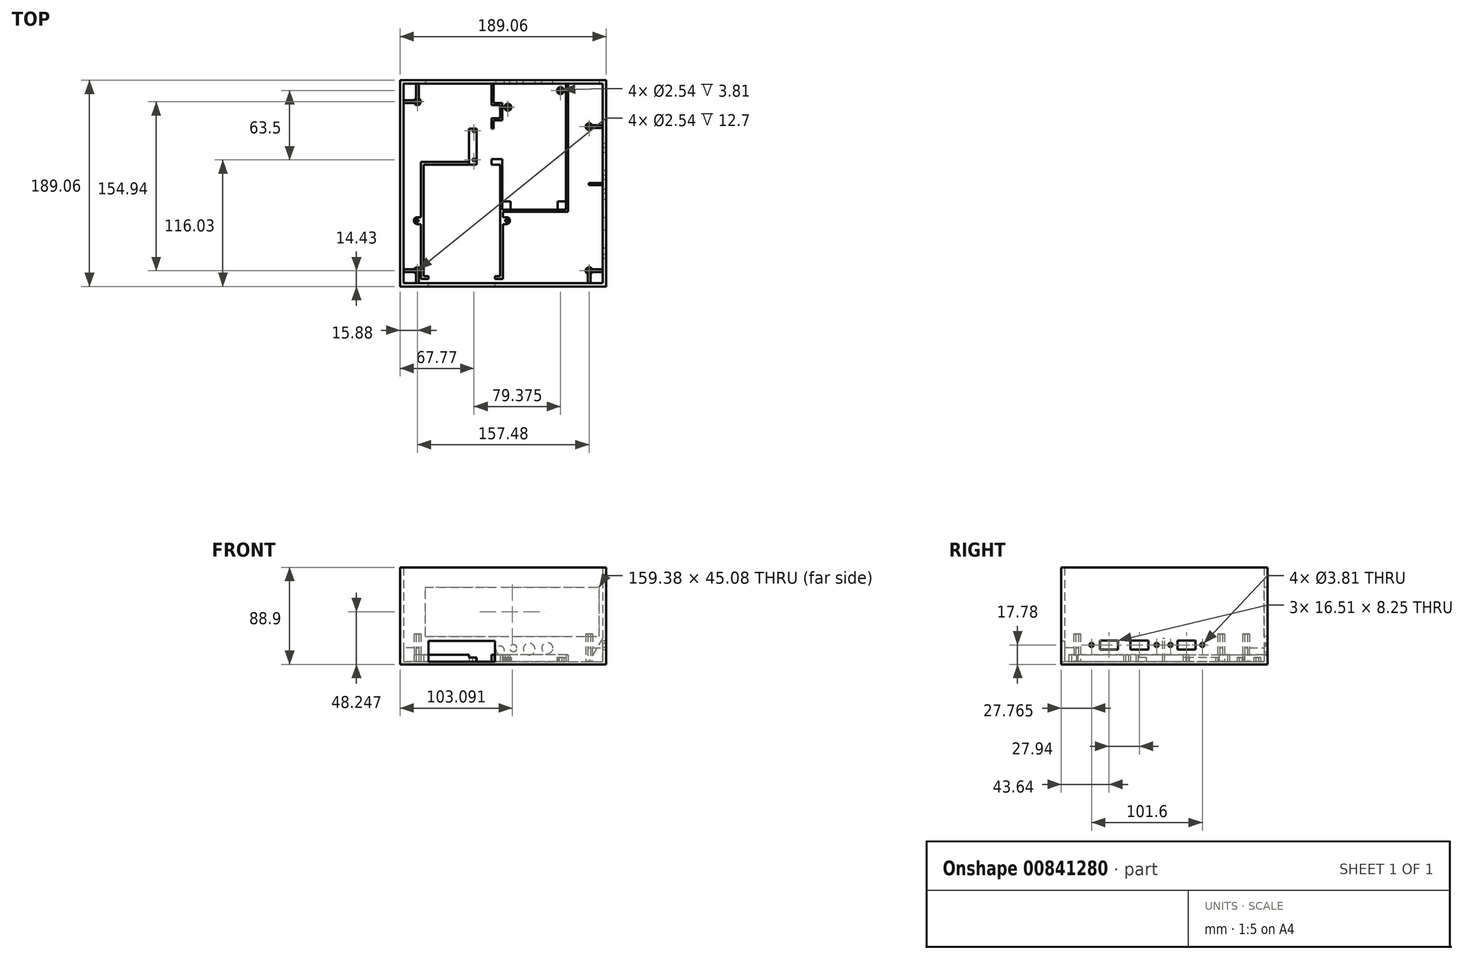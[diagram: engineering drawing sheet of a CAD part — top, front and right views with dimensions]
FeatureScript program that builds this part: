
annotation { "Feature Type Name" : "Feature", "Feature Type Description" : "" }
export const myFeature = defineFeature(function(context is Context, id is Id, definition is map)
    precondition{}
    {
        {
            var Q0;
            Q0=qCreatedBy(makeId("Top.planeOp"),FACE);
            var sketch = newSketch(context, id + "F0", { "sketchPlane" : qUnion([Q0])});
            skLineSegment(sketch, "E0.bottom", {"start": v(-6.35, 10.16) * mm, "end": v(163.65, 10.16) * mm});
            skLineSegment(sketch, "E0.top", {"start": v(-6.35, -159.84) * mm, "end": v(163.65, -159.84) * mm});
            skLineSegment(sketch, "E0.left", {"start": v(-6.35, 10.16) * mm, "end": v(-6.35, -159.84) * mm});
            skLineSegment(sketch, "E0.right", {"start": v(163.65, 10.16) * mm, "end": v(163.65, -159.84) * mm});
            skPoint(sketch, "E1", {"position": v(0, -154.94) * mm});
            skPoint(sketch, "E2", {"position": v(157.48, -22.86) * mm});
            skPoint(sketch, "E3", {"position": v(157.48, -154.94) * mm});
            skCircle(sketch, "E4", {"center": v(0, -154.94) * mm, "radius": 3.18 * mm});
            skCircle(sketch, "E5", {"center": v(0, 0) * mm, "radius": 3.18 * mm});
            skCircle(sketch, "E6", {"center": v(157.48, -22.86) * mm, "radius": 3.18 * mm});
            skCircle(sketch, "E7", {"center": v(157.48, -154.94) * mm, "radius": 3.18 * mm});
            skSolve(sketch);
        }
        {
            var Q0;
            Q0=qCreatedBy(makeId("Top.planeOp"),FACE);
            var sketch = newSketch(context, id + "F1", { "sketchPlane" : qUnion([Q0])});
            skLineSegment(sketch, "E8.0", {"start": v(-12.7, 16.51) * mm, "end": v(170, 16.51) * mm});
            skLineSegment(sketch, "E8.1", {"start": v(-12.7, 16.51) * mm, "end": v(-12.7, -166.2) * mm});
            skLineSegment(sketch, "E8.2", {"start": v(-12.7, -166.2) * mm, "end": v(170, -166.2) * mm});
            skLineSegment(sketch, "E8.3", {"start": v(170, 16.51) * mm, "end": v(170, -166.2) * mm});
            skLineSegment(sketch, "E9.0", {"start": v(-15.88, 19.69) * mm, "end": v(173.18, 19.69) * mm});
            skLineSegment(sketch, "E9.1", {"start": v(-15.88, 19.69) * mm, "end": v(-15.88, -169.37) * mm});
            skLineSegment(sketch, "E9.2", {"start": v(-15.88, -169.37) * mm, "end": v(173.18, -169.37) * mm});
            skLineSegment(sketch, "E9.3", {"start": v(173.18, 19.69) * mm, "end": v(173.18, -169.37) * mm});
            skSolve(sketch);
        }
        {
            var Q0;
            Q0=qSketchRegion(id+"F1",true);
            extrude(context, id + "F2", {"entities" : qUnion([Q0]), "depth" : 86.36 * mm, "offsetDistance" : 25.4 * mm});
        }
        {
            var Q0;
            Q0=qCreatedBy(makeId("Top.planeOp"),FACE);
            var sketch = newSketch(context, id + "F3", { "sketchPlane" : qUnion([Q0])});
            skLineSegment(sketch, "E10.bottom", {"start": v(135.08, -97.79) * mm, "end": v(135.08, 15.24) * mm, "construction": true});
            skLineSegment(sketch, "E10.top", {"start": v(79.2, -18.41) * mm, "end": v(79.2, 0) * mm, "construction": true});
            skLineSegment(sketch, "E10.left", {"start": v(135.08, 15.24) * mm, "end": v(79.2, 15.24) * mm, "construction": true});
            skLineSegment(sketch, "E10.right", {"start": v(135.08, -97.79) * mm, "end": v(79.2, -97.79) * mm, "construction": true});
            skCircle(sketch, "E11", {"center": v(131.27, 10.16) * mm, "radius": 1.27 * mm});
            skCircle(sketch, "E12", {"center": v(131.27, 10.16) * mm, "radius": 3.18 * mm});
            skLineSegment(sketch, "E13", {"start": v(79.2, 15.24) * mm, "end": v(71.07, 15.24) * mm, "construction": true});
            skLineSegment(sketch, "E14", {"start": v(71.07, 15.24) * mm, "end": v(71.07, 0) * mm, "construction": true});
            skLineSegment(sketch, "E15", {"start": v(71.07, 0) * mm, "end": v(79.2, 0) * mm, "construction": true});
            skLineSegment(sketch, "E16", {"start": v(79.2, -18.41) * mm, "end": v(71.07, -18.41) * mm, "construction": true});
            skLineSegment(sketch, "E17", {"start": v(71.07, -18.41) * mm, "end": v(71.07, -50.16) * mm, "construction": true});
            skLineSegment(sketch, "E18", {"start": v(71.07, -50.16) * mm, "end": v(79.2, -50.16) * mm, "construction": true});
            skCircle(sketch, "E19", {"center": v(83, -5.08) * mm, "radius": 3.18 * mm});
            skCircle(sketch, "E20", {"center": v(83, -5.08) * mm, "radius": 1.27 * mm});
            skLineSegment(sketch, "E21.trimOffspring", {"start": v(79.2, -97.79) * mm, "end": v(79.2, -50.16) * mm, "construction": true});
            skLineSegment(sketch, "E22.0", {"start": v(77.93, -17.14) * mm, "end": v(77.93, -1.27) * mm});
            skLineSegment(sketch, "E22.1", {"start": v(77.93, -17.14) * mm, "end": v(69.8, -17.14) * mm});
            skLineSegment(sketch, "E22.4", {"start": v(77.93, -99.06) * mm, "end": v(77.93, -52.7) * mm});
            skLineSegment(sketch, "E22.5", {"start": v(69.8, -1.27) * mm, "end": v(77.93, -1.27) * mm});
            skLineSegment(sketch, "E22.6", {"start": v(69.8, 16.51) * mm, "end": v(69.8, -1.27) * mm});
            skLineSegment(sketch, "E22.8", {"start": v(136.35, 16.51) * mm, "end": v(69.8, 16.51) * mm});
            skLineSegment(sketch, "E22.9", {"start": v(136.35, -99.06) * mm, "end": v(136.35, 16.51) * mm});
            skLineSegment(sketch, "E22.10", {"start": v(136.35, -99.06) * mm, "end": v(77.93, -99.06) * mm});
            skLineSegment(sketch, "E23.bottom", {"start": v(77.93, -99.06) * mm, "end": v(77.93, -91.44) * mm});
            skLineSegment(sketch, "E23.top", {"start": v(85.55, -99.06) * mm, "end": v(85.55, -91.44) * mm});
            skLineSegment(sketch, "E23.left", {"start": v(77.93, -99.06) * mm, "end": v(85.55, -99.06) * mm});
            skLineSegment(sketch, "E23.right", {"start": v(77.93, -91.44) * mm, "end": v(85.55, -91.44) * mm});
            skLineSegment(sketch, "E24.bottom", {"start": v(136.35, -99.06) * mm, "end": v(136.35, -91.44) * mm});
            skLineSegment(sketch, "E24.top", {"start": v(128.73, -99.06) * mm, "end": v(128.73, -91.44) * mm});
            skLineSegment(sketch, "E24.left", {"start": v(136.35, -99.06) * mm, "end": v(128.73, -99.06) * mm});
            skLineSegment(sketch, "E24.right", {"start": v(136.35, -91.44) * mm, "end": v(128.73, -91.44) * mm});
            skLineSegment(sketch, "E25.0", {"start": v(138.25, -100.96) * mm, "end": v(76.02, -100.96) * mm});
            skLineSegment(sketch, "E25.1", {"start": v(138.25, -100.96) * mm, "end": v(138.25, 18.42) * mm});
            skLineSegment(sketch, "E25.2", {"start": v(76.02, -100.96) * mm, "end": v(76.02, -57.78) * mm});
            skLineSegment(sketch, "E25.3", {"start": v(138.25, 18.42) * mm, "end": v(67.9, 18.42) * mm});
            skLineSegment(sketch, "E25.4", {"start": v(67.9, 18.42) * mm, "end": v(67.9, -3.17) * mm});
            skLineSegment(sketch, "E25.5", {"start": v(67.9, -3.17) * mm, "end": v(76.02, -3.17) * mm});
            skLineSegment(sketch, "E25.7", {"start": v(67.9, -15.24) * mm, "end": v(67.9, -24.76) * mm});
            skLineSegment(sketch, "E25.8", {"start": v(76.02, -15.24) * mm, "end": v(67.9, -15.24) * mm});
            skLineSegment(sketch, "E25.9", {"start": v(76.02, -15.24) * mm, "end": v(76.02, -3.17) * mm});
            skLineSegment(sketch, "E26", {"start": v(76.02, -57.78) * mm, "end": v(47.45, -57.78) * mm});
            skLineSegment(sketch, "E27", {"start": v(69.8, -17.14) * mm, "end": v(69.8, -27.94) * mm});
            skCircle(sketch, "E28", {"center": v(51.9, -53.34) * mm, "radius": 1.27 * mm});
            skLineSegment(sketch, "E29", {"start": v(54.43, -52.7) * mm, "end": v(54.43, -27.94) * mm});
            skLineSegment(sketch, "E30", {"start": v(54.43, -52.7) * mm, "end": v(77.93, -52.7) * mm});
            skLineSegment(sketch, "E31", {"start": v(54.43, -27.94) * mm, "end": v(69.8, -27.94) * mm});
            skCircle(sketch, "E32", {"center": v(51.9, -26.67) * mm, "radius": 1.27 * mm});
            skLineSegment(sketch, "E33", {"start": v(47.45, -57.78) * mm, "end": v(47.45, -24.76) * mm});
            skLineSegment(sketch, "E34", {"start": v(47.45, -24.76) * mm, "end": v(67.9, -24.76) * mm});
            skLineSegment(sketch, "E35", {"start": v(54.43, -52.7) * mm, "end": v(54.43, -57.78) * mm});
            skLineSegment(sketch, "E36", {"start": v(54.43, -27.94) * mm, "end": v(54.43, -24.76) * mm});
            skLineSegment(sketch, "E37", {"start": v(136.35, 16.51) * mm, "end": v(138.25, 16.51) * mm});
            skLineSegment(sketch, "E38", {"start": v(69.8, 16.51) * mm, "end": v(67.9, 16.51) * mm});
            skLineSegment(sketch, "E39", {"start": v(67.9, -52.7) * mm, "end": v(67.9, -57.78) * mm});
            skLineSegment(sketch, "E40", {"start": v(67.9, -24.76) * mm, "end": v(69.8, -24.76) * mm});
            skSolve(sketch);
        }
        {
            var Q0;
            Q0=qCreatedBy(makeId("Top.planeOp"),FACE);
            var sketch = newSketch(context, id + "F4", { "sketchPlane" : qUnion([Q0])});
            skLineSegment(sketch, "E41.bottom", {"start": v(5.66, -57.78) * mm, "end": v(76.02, -57.78) * mm});
            skLineSegment(sketch, "E41.top", {"start": v(5.66, -159.84) * mm, "end": v(76.02, -159.84) * mm});
            skLineSegment(sketch, "E41.left", {"start": v(5.66, -57.78) * mm, "end": v(5.66, -159.84) * mm});
            skLineSegment(sketch, "E41.right", {"start": v(76.02, -57.78) * mm, "end": v(76.02, -159.84) * mm});
            skLineSegment(sketch, "E42.0", {"start": v(3.12, -55.24) * mm, "end": v(47.45, -55.24) * mm});
            skLineSegment(sketch, "E42.1", {"start": v(3.12, -55.24) * mm, "end": v(3.12, -105.86) * mm});
            skLineSegment(sketch, "E42.2", {"start": v(3.12, -162.38) * mm, "end": v(10.36, -162.38) * mm});
            skLineSegment(sketch, "E42.3", {"start": v(78.56, -100.96) * mm, "end": v(78.56, -105.86) * mm});
            skLineSegment(sketch, "E43", {"start": v(47.45, -55.24) * mm, "end": v(47.45, -57.78) * mm});
            skLineSegment(sketch, "E44", {"start": v(76.02, -100.96) * mm, "end": v(78.56, -100.96) * mm});
            skLineSegment(sketch, "E45", {"start": v(10.36, -162.38) * mm, "end": v(10.36, -159.84) * mm});
            skLineSegment(sketch, "E46", {"start": v(40.84, -162.38) * mm, "end": v(40.84, -159.84) * mm, "construction": true});
            skLineSegment(sketch, "E47.MirrorCS", {"start": v(71.32, -162.38) * mm, "end": v(71.32, -159.84) * mm});
            skLineSegment(sketch, "E48.trimOffspring", {"start": v(71.32, -162.38) * mm, "end": v(78.56, -162.38) * mm});
            skArc(sketch, "E49", {"start": v(81.74, -112.21) * mm, "mid": v(84.91, -109.04) * mm, "end": v(81.74, -105.86) * mm});
            skLineSegment(sketch, "E50", {"start": v(81.74, -105.86) * mm, "end": v(81.74, -112.21) * mm, "construction": true});
            skLineSegment(sketch, "E51", {"start": v(81.74, -112.21) * mm, "end": v(78.56, -112.21) * mm});
            skLineSegment(sketch, "E52", {"start": v(81.74, -105.86) * mm, "end": v(78.56, -105.86) * mm});
            skLineSegment(sketch, "E53.trimOffspring", {"start": v(78.56, -112.21) * mm, "end": v(78.56, -162.38) * mm});
            skLineSegment(sketch, "E54.MirrorCS", {"start": v(-0.05, -105.86) * mm, "end": v(3.12, -105.86) * mm});
            skLineSegment(sketch, "E55.MirrorCS", {"start": v(-0.05, -112.21) * mm, "end": v(3.12, -112.21) * mm});
            skArc(sketch, "E56.MirrorCS", {"start": v(-0.05, -112.21) * mm, "mid": v(-3.23, -109.04) * mm, "end": v(-0.05, -105.86) * mm});
            skLineSegment(sketch, "E57.trimOffspring", {"start": v(3.12, -112.21) * mm, "end": v(3.12, -162.38) * mm});
            skCircle(sketch, "E58", {"center": v(81.74, -109.04) * mm, "radius": 1.27 * mm});
            skCircle(sketch, "E59", {"center": v(-0.05, -109.04) * mm, "radius": 1.27 * mm});
            skSolve(sketch);
        }
        {
            var Q0;
            Q0=qCreatedBy(makeId("Top.planeOp"),FACE);
            var sketch = newSketch(context, id + "F5", { "sketchPlane" : qUnion([Q0])});
            skLineSegment(sketch, "E60.bottom", {"start": v(-15.88, 19.69) * mm, "end": v(173.18, 19.69) * mm});
            skLineSegment(sketch, "E60.top", {"start": v(-15.88, -169.37) * mm, "end": v(173.18, -169.37) * mm});
            skLineSegment(sketch, "E60.left", {"start": v(-15.88, 19.69) * mm, "end": v(-15.88, -169.37) * mm});
            skLineSegment(sketch, "E60.right", {"start": v(173.18, 19.69) * mm, "end": v(173.18, -169.37) * mm});
            skSolve(sketch);
        }
        {
            var Q0;
            Q0=qSketchRegion(id+"F5",true);
            extrude(context, id + "F6", {"entities" : qUnion([Q0]), "operationType" : NewBodyOperationType.ADD, "oppositeDirection" : true, "depth" : 2.54 * mm, "offsetDistance" : 25.4 * mm});
        }
        {
            var Q0;
            Q0=qCreatedBy(makeId("Top.planeOp"),FACE);
            var sketch = newSketch(context, id + "F7", { "sketchPlane" : qUnion([Q0])});
            skLineSegment(sketch, "E61.bottom", {"start": v(77.93, -91.44) * mm, "end": v(85.55, -91.44) * mm});
            skLineSegment(sketch, "E61.top", {"start": v(77.93, -99.06) * mm, "end": v(85.55, -99.06) * mm});
            skLineSegment(sketch, "E61.left", {"start": v(77.93, -91.44) * mm, "end": v(77.93, -99.06) * mm});
            skLineSegment(sketch, "E61.right", {"start": v(85.55, -91.44) * mm, "end": v(85.55, -99.06) * mm});
            skLineSegment(sketch, "E62.bottom", {"start": v(128.73, -91.44) * mm, "end": v(136.35, -91.44) * mm});
            skLineSegment(sketch, "E62.top", {"start": v(128.73, -99.06) * mm, "end": v(136.35, -99.06) * mm});
            skLineSegment(sketch, "E62.left", {"start": v(128.73, -91.44) * mm, "end": v(128.73, -99.06) * mm});
            skLineSegment(sketch, "E62.right", {"start": v(136.35, -91.44) * mm, "end": v(136.35, -99.06) * mm});
            skCircle(sketch, "E63.0", {"center": v(83, -5.08) * mm, "radius": 3.18 * mm});
            skCircle(sketch, "E63.1", {"center": v(131.27, 10.16) * mm, "radius": 3.18 * mm});
            skCircle(sketch, "E64.0", {"center": v(83, -5.08) * mm, "radius": 1.27 * mm});
            skCircle(sketch, "E64.1", {"center": v(131.27, 10.16) * mm, "radius": 1.27 * mm});
            skLineSegment(sketch, "E65.bottom", {"start": v(47.45, -24.76) * mm, "end": v(54.43, -24.76) * mm});
            skLineSegment(sketch, "E65.top", {"start": v(47.45, -57.78) * mm, "end": v(54.43, -57.78) * mm});
            skLineSegment(sketch, "E65.left", {"start": v(47.45, -24.76) * mm, "end": v(47.45, -57.78) * mm});
            skLineSegment(sketch, "E65.right", {"start": v(54.43, -24.76) * mm, "end": v(54.43, -57.78) * mm});
            skCircle(sketch, "E66.1", {"center": v(51.9, -26.67) * mm, "radius": 1.27 * mm});
            skCircle(sketch, "E66.2", {"center": v(51.9, -53.34) * mm, "radius": 1.27 * mm});
            skSolve(sketch);
        }
        {
            var Q0;
            Q0=qSketchRegion(id+"F7",true);
            extrude(context, id + "F8", {"entities" : qUnion([Q0]), "operationType" : NewBodyOperationType.ADD, "depth" : 3.8 * mm, "offsetDistance" : 25.4 * mm});
        }
        {
            var Q0;
            Q0=qCreatedBy(makeId("Top.planeOp"),FACE);
            var sketch = newSketch(context, id + "F9", { "sketchPlane" : qUnion([Q0])});
            skLineSegment(sketch, "E67.0", {"start": v(67.9, -15.24) * mm, "end": v(67.9, -24.76) * mm});
            skLineSegment(sketch, "E67.1", {"start": v(67.9, -24.76) * mm, "end": v(69.8, -24.76) * mm});
            skLineSegment(sketch, "E67.2", {"start": v(69.8, -17.14) * mm, "end": v(69.8, -24.76) * mm});
            skLineSegment(sketch, "E67.3", {"start": v(76.02, -15.24) * mm, "end": v(67.9, -15.24) * mm});
            skLineSegment(sketch, "E67.4", {"start": v(77.93, -17.14) * mm, "end": v(69.8, -17.14) * mm});
            skLineSegment(sketch, "E67.5", {"start": v(77.93, -17.14) * mm, "end": v(77.93, -1.27) * mm});
            skLineSegment(sketch, "E67.6", {"start": v(76.02, -15.24) * mm, "end": v(76.02, -3.17) * mm});
            skLineSegment(sketch, "E67.7", {"start": v(69.8, -1.27) * mm, "end": v(77.93, -1.27) * mm});
            skLineSegment(sketch, "E67.8", {"start": v(67.9, -3.17) * mm, "end": v(76.02, -3.17) * mm});
            skLineSegment(sketch, "E67.9", {"start": v(67.9, 16.51) * mm, "end": v(67.9, -3.17) * mm});
            skLineSegment(sketch, "E67.10", {"start": v(69.8, 16.51) * mm, "end": v(69.8, -1.27) * mm});
            skLineSegment(sketch, "E67.13", {"start": v(136.35, -99.06) * mm, "end": v(136.35, 16.51) * mm});
            skLineSegment(sketch, "E67.14", {"start": v(138.25, -100.96) * mm, "end": v(138.25, 16.51) * mm});
            skLineSegment(sketch, "E67.15", {"start": v(136.35, -99.06) * mm, "end": v(77.93, -99.06) * mm});
            skLineSegment(sketch, "E67.16", {"start": v(138.25, -100.96) * mm, "end": v(78.56, -100.96) * mm});
            skLineSegment(sketch, "E67.17", {"start": v(78.56, -100.96) * mm, "end": v(78.56, -105.86) * mm});
            skLineSegment(sketch, "E67.18", {"start": v(81.74, -105.86) * mm, "end": v(78.56, -105.86) * mm});
            skArc(sketch, "E67.19", {"start": v(81.74, -112.21) * mm, "mid": v(84.91, -109.04) * mm, "end": v(81.74, -105.86) * mm});
            skLineSegment(sketch, "E67.20.1", {"start": v(76.02, -100.96) * mm, "end": v(76.02, -159.84) * mm});
            skLineSegment(sketch, "E67.20.2", {"start": v(76.02, -159.84) * mm, "end": v(71.32, -159.84) * mm});
            skLineSegment(sketch, "E67.20.3", {"start": v(71.32, -159.84) * mm, "end": v(71.32, -162.38) * mm});
            skLineSegment(sketch, "E67.20.4", {"start": v(71.32, -162.38) * mm, "end": v(78.56, -162.38) * mm});
            skLineSegment(sketch, "E67.20.5", {"start": v(78.56, -162.38) * mm, "end": v(78.56, -112.21) * mm});
            skLineSegment(sketch, "E67.20.6", {"start": v(78.56, -112.21) * mm, "end": v(81.74, -112.21) * mm});
            skArc(sketch, "E67.20.7", {"start": v(81.74, -112.21) * mm, "mid": v(84.91, -109.04) * mm, "end": v(81.74, -105.86) * mm});
            skLineSegment(sketch, "E67.20.8", {"start": v(81.74, -105.86) * mm, "end": v(78.56, -105.86) * mm});
            skLineSegment(sketch, "E67.20.9", {"start": v(78.56, -105.86) * mm, "end": v(78.56, -100.96) * mm});
            skLineSegment(sketch, "E67.21.0", {"start": v(47.45, -57.78) * mm, "end": v(47.45, -55.24) * mm});
            skLineSegment(sketch, "E67.21.1", {"start": v(47.45, -55.24) * mm, "end": v(3.12, -55.24) * mm});
            skLineSegment(sketch, "E67.21.2", {"start": v(3.12, -55.24) * mm, "end": v(3.12, -105.86) * mm});
            skLineSegment(sketch, "E67.21.3", {"start": v(3.12, -105.86) * mm, "end": v(-0.05, -105.86) * mm});
            skArc(sketch, "E67.21.4", {"start": v(-0.05, -105.86) * mm, "mid": v(-3.23, -109.04) * mm, "end": v(-0.05, -112.21) * mm});
            skLineSegment(sketch, "E67.21.5", {"start": v(-0.05, -112.21) * mm, "end": v(3.12, -112.21) * mm});
            skLineSegment(sketch, "E67.21.6", {"start": v(3.12, -112.21) * mm, "end": v(3.12, -162.38) * mm});
            skLineSegment(sketch, "E67.21.7", {"start": v(3.12, -162.38) * mm, "end": v(10.36, -162.38) * mm});
            skLineSegment(sketch, "E67.21.8", {"start": v(10.36, -162.38) * mm, "end": v(10.36, -159.84) * mm});
            skLineSegment(sketch, "E67.21.9", {"start": v(10.36, -159.84) * mm, "end": v(5.66, -159.84) * mm});
            skLineSegment(sketch, "E67.21.10", {"start": v(5.66, -159.84) * mm, "end": v(5.66, -57.78) * mm});
            skLineSegment(sketch, "E67.21.11", {"start": v(5.66, -57.78) * mm, "end": v(47.45, -57.78) * mm});
            skLineSegment(sketch, "E67.22", {"start": v(76.02, -100.96) * mm, "end": v(76.02, -57.78) * mm});
            skLineSegment(sketch, "E67.23", {"start": v(77.93, -99.06) * mm, "end": v(77.93, -52.7) * mm});
            skLineSegment(sketch, "E67.24", {"start": v(67.9, -52.7) * mm, "end": v(77.93, -52.7) * mm});
            skLineSegment(sketch, "E67.25", {"start": v(67.9, -52.7) * mm, "end": v(67.9, -57.78) * mm});
            skLineSegment(sketch, "E67.26", {"start": v(76.02, -57.78) * mm, "end": v(67.9, -57.78) * mm});
            skPoint(sketch, "E68.orphan", {"position": v(69.8, -27.94) * mm});
            skPoint(sketch, "E69.orphan", {"position": v(54.43, -52.7) * mm});
            skPoint(sketch, "E70.orphan", {"position": v(47.45, -57.78) * mm});
            skPoint(sketch, "E71.orphan", {"position": v(76.02, -100.96) * mm});
            skLineSegment(sketch, "E72.0", {"start": v(67.9, 16.51) * mm, "end": v(69.8, 16.51) * mm});
            skPoint(sketch, "E73.orphan", {"position": v(-12.7, 16.51) * mm});
            skPoint(sketch, "E74.orphan", {"position": v(170, 16.51) * mm});
            skPoint(sketch, "E75.orphan", {"position": v(138.25, 18.42) * mm});
            skPoint(sketch, "E76.orphan", {"position": v(67.9, 18.42) * mm});
            skLineSegment(sketch, "E77.trimOffspring", {"start": v(136.35, 16.51) * mm, "end": v(138.25, 16.51) * mm});
            skCircle(sketch, "E78.0", {"center": v(-0.05, -109.04) * mm, "radius": 1.27 * mm});
            skCircle(sketch, "E78.1", {"center": v(81.74, -109.04) * mm, "radius": 1.27 * mm});
            skSolve(sketch);
        }
        {
            var Q0;
            Q0=qSketchRegion(id+"F9",true);
            extrude(context, id + "F10", {"entities" : qUnion([Q0]), "operationType" : NewBodyOperationType.ADD, "depth" : 6.35 * mm, "offsetDistance" : 25.4 * mm});
        }
        {
            var Q0;
            Q0=makeQuery(id+"F6.boolean.opBoolean","MERGE",FACE,{"derivedFrom":[makeQuery(id+"F2.opExtrude","SWEPT_FACE",FACE,{"disambiguationData":[OSD([sQuery(id+"F1.wireOp",EDGE,"E9.0")])]}),makeQuery(id+"F6.opExtrude","SWEPT_FACE",FACE,{"disambiguationData":[OSD([sQuery(id+"F5.wireOp",EDGE,"E60.bottom")])]})]});
            var sketch = newSketch(context, id + "F11", { "sketchPlane" : qUnion([Q0])});
            skCircle(sketch, "E79", {"center": v(-119.2, 12.32) * mm, "radius": 5.08 * mm});
            skCircle(sketch, "E80", {"center": v(-102.56, 11.43) * mm, "radius": 5.4 * mm});
            skCircle(sketch, "E81", {"center": v(-88.09, 12.32) * mm, "radius": 3.18 * mm});
            skCircle(sketch, "E82", {"center": v(-75.9, 10.41) * mm, "radius": 3.81 * mm});
            skLineSegment(sketch, "E83", {"start": v(-54.43, 3.81) * mm, "end": v(-135.08, 3.81) * mm, "construction": true});
            skLineSegment(sketch, "E84", {"start": v(-135.08, 3.81) * mm, "end": v(-135.08, 0) * mm, "construction": true});
            skSolve(sketch);
        }
        {
            var Q0;
            Q0=qSketchRegion(id+"F11",true);
            extrude(context, id + "F12", {"entities" : qUnion([Q0]), "operationType" : NewBodyOperationType.REMOVE, "endBound" : BoundingType.UP_TO_NEXT, "oppositeDirection" : true, "depth" : 25.4 * mm, "offsetDistance" : 25.4 * mm});
        }
        {
            var Q0;
            Q0=makeQuery(id+"F2.opExtrude","SWEPT_FACE",FACE,{"disambiguationData":[OSD([sQuery(id+"F1.wireOp",EDGE,"E8.2")])]});
            var sketch = newSketch(context, id + "F13", { "sketchPlane" : qUnion([Q0])});
            skLineSegment(sketch, "E85.0", {"start": v(-10.36, 6.35) * mm, "end": v(-10.36, 0) * mm});
            skLineSegment(sketch, "E85.1", {"start": v(-71.32, 6.35) * mm, "end": v(-71.32, 0) * mm});
            skLineSegment(sketch, "E86", {"start": v(-10.36, 6.35) * mm, "end": v(-71.32, 6.35) * mm, "construction": true});
            skLineSegment(sketch, "E87", {"start": v(-10.36, 0) * mm, "end": v(-71.32, 0) * mm});
            skLineSegment(sketch, "E88", {"start": v(-10.36, 6.35) * mm, "end": v(-10.36, 19.05) * mm});
            skLineSegment(sketch, "E89", {"start": v(-10.36, 19.05) * mm, "end": v(-71.32, 19.05) * mm});
            skLineSegment(sketch, "E90", {"start": v(-71.32, 19.05) * mm, "end": v(-71.32, 6.35) * mm});
            skLineSegment(sketch, "E91", {"start": v(-16.71, 19.05) * mm, "end": v(-16.71, 0) * mm, "construction": true});
            skLineSegment(sketch, "E92", {"start": v(-17.47, 19.05) * mm, "end": v(-17.47, 0) * mm, "construction": true});
            skLineSegment(sketch, "E93.1.0.0", {"start": v(-28.14, 19.05) * mm, "end": v(-28.14, 0) * mm, "construction": true});
            skLineSegment(sketch, "E93.1.0.1", {"start": v(-28.9, 19.05) * mm, "end": v(-28.9, 0) * mm, "construction": true});
            skLineSegment(sketch, "E93.2.0.0", {"start": v(-39.57, 19.05) * mm, "end": v(-39.57, 0) * mm, "construction": true});
            skLineSegment(sketch, "E93.2.0.1", {"start": v(-40.33, 19.05) * mm, "end": v(-40.33, 0) * mm, "construction": true});
            skLineSegment(sketch, "E93.3.0.0", {"start": v(-51, 19.05) * mm, "end": v(-51, 0) * mm, "construction": true});
            skLineSegment(sketch, "E93.3.0.1", {"start": v(-51.76, 19.05) * mm, "end": v(-51.76, 0) * mm, "construction": true});
            skLineSegment(sketch, "E93.4.0.0", {"start": v(-62.43, 19.05) * mm, "end": v(-62.43, 0) * mm, "construction": true});
            skLineSegment(sketch, "E93.4.0.1", {"start": v(-63.2, 19.05) * mm, "end": v(-63.2, 0) * mm, "construction": true});
            skLineSegment(sketch, "E93.direction1", {"start": v(-17.47, 0) * mm, "end": v(-28.9, 0) * mm, "construction": true});
            skSolve(sketch);
        }
        {
            var Q0;
            {var subQ4=sQuery(id+"F13.wireOp",EDGE,"E85.0");Q0=makeQuery(id+"F13.imprint","IMPRINT",FACE,{"disambiguationData":[TD([[makeQuery(id+"F13.imprint","IMPRINT",EDGE,{"derivedFrom":subQ4}),-1.0]])]});}
            var Q1;
            {var subQ0=sQuery(id+"F13.wireOp",EDGE,"E92");Q1=makeQuery(id+"F13.imprint","IMPRINT",FACE,{"disambiguationData":[TD([[makeQuery(id+"F13.imprint","IMPRINT",EDGE,{"derivedFrom":subQ0}),-1.0]])]});}
            var Q2;
            {var subQ0=sQuery(id+"F13.wireOp",EDGE,"E93.1.0.1");Q2=makeQuery(id+"F13.imprint","IMPRINT",FACE,{"disambiguationData":[TD([[makeQuery(id+"F13.imprint","IMPRINT",EDGE,{"derivedFrom":subQ0}),-1.0]])]});}
            var Q3;
            {var subQ0=sQuery(id+"F13.wireOp",EDGE,"E93.2.0.1");Q3=makeQuery(id+"F13.imprint","IMPRINT",FACE,{"disambiguationData":[TD([[makeQuery(id+"F13.imprint","IMPRINT",EDGE,{"derivedFrom":subQ0}),-1.0]])]});}
            var Q4;
            {var subQ0=sQuery(id+"F13.wireOp",EDGE,"E93.3.0.1");Q4=makeQuery(id+"F13.imprint","IMPRINT",FACE,{"disambiguationData":[TD([[makeQuery(id+"F13.imprint","IMPRINT",EDGE,{"derivedFrom":subQ0}),-1.0]])]});}
            var Q5;
            {var subQ4=sQuery(id+"F13.wireOp",EDGE,"E85.1");Q5=makeQuery(id+"F13.imprint","IMPRINT",FACE,{"disambiguationData":[TD([[makeQuery(id+"F13.imprint","IMPRINT",EDGE,{"derivedFrom":subQ4}),1.0]])]});}
            extrude(context, id + "F14", {"entities" : qUnion([Q0, Q1, Q2, Q3, Q4, Q5]), "operationType" : NewBodyOperationType.REMOVE, "endBound" : BoundingType.THROUGH_ALL, "oppositeDirection" : true, "depth" : 2.54 * mm, "offsetDistance" : 25.4 * mm});
        }
        {
            var Q0;
            Q0=makeQuery(id+"F6.boolean.opBoolean","MERGE",FACE,{"derivedFrom":[makeQuery(id+"F2.opExtrude","SWEPT_FACE",FACE,{"disambiguationData":[OSD([sQuery(id+"F1.wireOp",EDGE,"E9.3")])]}),makeQuery(id+"F6.opExtrude","SWEPT_FACE",FACE,{"disambiguationData":[OSD([sQuery(id+"F5.wireOp",EDGE,"E60.right")])]})]});
            var sketch = newSketch(context, id + "F15", { "sketchPlane" : qUnion([Q0])});
            skLineSegment(sketch, "E94.bottom", {"start": v(-149.86, 8.9) * mm, "end": v(-25.4, 8.9) * mm, "construction": true});
            skLineSegment(sketch, "E94.top", {"start": v(-149.86, 21.59) * mm, "end": v(-25.4, 21.59) * mm, "construction": true});
            skLineSegment(sketch, "E94.left", {"start": v(-149.86, 8.9) * mm, "end": v(-149.86, 21.6) * mm, "construction": true});
            skLineSegment(sketch, "E94.right", {"start": v(-25.4, 8.9) * mm, "end": v(-25.4, 21.59) * mm, "construction": true});
            skLineSegment(sketch, "E95", {"start": v(-111.76, 21.6) * mm, "end": v(-111.76, 8.9) * mm, "construction": true});
            skLineSegment(sketch, "E96.bottom", {"start": v(-117.47, 19.37) * mm, "end": v(-133.98, 19.37) * mm});
            skLineSegment(sketch, "E96.top", {"start": v(-117.47, 11.11) * mm, "end": v(-133.98, 11.11) * mm});
            skLineSegment(sketch, "E96.left", {"start": v(-117.47, 19.37) * mm, "end": v(-117.47, 11.11) * mm});
            skLineSegment(sketch, "E96.right", {"start": v(-133.98, 19.37) * mm, "end": v(-133.98, 11.11) * mm});
            skPoint(sketch, "E96.middle", {"position": v(-125.73, 15.24) * mm});
            skPoint(sketch, "E97", {"position": v(-111.76, 15.24) * mm});
            skCircle(sketch, "E98", {"center": v(-141.6, 15.24) * mm, "radius": 1.9 * mm});
            skPoint(sketch, "E98.centerSnap0", {"position": v(-133.98, 15.24) * mm});
            skLineSegment(sketch, "E99.MirrorCS", {"start": v(-106.04, 19.37) * mm, "end": v(-106.04, 11.11) * mm});
            skLineSegment(sketch, "E100.MirrorCS", {"start": v(-106.04, 19.37) * mm, "end": v(-89.53, 19.37) * mm});
            skLineSegment(sketch, "E101.MirrorCS", {"start": v(-89.53, 19.37) * mm, "end": v(-89.53, 11.11) * mm});
            skPoint(sketch, "E102.MirrorP", {"position": v(-89.53, 15.24) * mm});
            skCircle(sketch, "E103.MirrorC", {"center": v(-81.91, 15.24) * mm, "radius": 1.9 * mm});
            skPoint(sketch, "E104.MirrorP", {"position": v(-97.79, 15.24) * mm});
            skLineSegment(sketch, "E105.MirrorCS", {"start": v(-106.04, 11.11) * mm, "end": v(-89.53, 11.11) * mm});
            skLineSegment(sketch, "E106", {"start": v(-54.6, 21.6) * mm, "end": v(-54.6, 8.9) * mm, "construction": true});
            skLineSegment(sketch, "E107.bottom", {"start": v(-46.35, 19.37) * mm, "end": v(-62.86, 19.37) * mm});
            skLineSegment(sketch, "E107.top", {"start": v(-46.35, 11.11) * mm, "end": v(-62.86, 11.11) * mm});
            skLineSegment(sketch, "E107.left", {"start": v(-46.35, 19.37) * mm, "end": v(-46.35, 11.11) * mm});
            skLineSegment(sketch, "E107.right", {"start": v(-62.86, 19.37) * mm, "end": v(-62.86, 11.11) * mm});
            skPoint(sketch, "E107.middle", {"position": v(-54.6, 15.24) * mm});
            skCircle(sketch, "E108", {"center": v(-69.22, 15.24) * mm, "radius": 1.9 * mm});
            skCircle(sketch, "E109.MirrorC", {"center": v(-40, 15.24) * mm, "radius": 1.9 * mm});
            skLineSegment(sketch, "E110", {"start": v(-75.56, 21.59) * mm, "end": v(-75.56, 8.9) * mm, "construction": true});
            skSolve(sketch);
        }
        {
            var Q0;
            Q0=qSketchRegion(id+"F15",true);
            extrude(context, id + "F16", {"entities" : qUnion([Q0]), "operationType" : NewBodyOperationType.REMOVE, "endBound" : BoundingType.UP_TO_NEXT, "oppositeDirection" : true, "depth" : 25.4 * mm, "offsetDistance" : 25.4 * mm});
        }
        {
            var Q0;
            Q0=sQuery(id+"F15.wireOp",EDGE,"E110");
            cPoint(context, id + "F17", {"entities" : qUnion([Q0]), "parameter" : 0.5});
        }
        {
            var Q0;
            Q0=qCreatedBy(makeId("Front.planeOp"),FACE);
            var Q1;
            Q1=qCreatedBy(id+"F17",VERTEX);
            cPlane(context, id + "F18", {"entities" : qUnion([Q0, Q1]), "cplaneType" : CPlaneType.PLANE_POINT, "offset" : 25.4 * mm, "width" : 152.4 * mm, "height" : 152.4 * mm});
        }
        {
            var Q0;
            Q0=qCreatedBy(id+"F18.planeOp",FACE);
            var sketch = newSketch(context, id + "F19", { "sketchPlane" : qUnion([Q0])});
            skLineSegment(sketch, "E111", {"start": v(170, 21.6) * mm, "end": v(157.3, 0) * mm});
            skLineSegment(sketch, "E112", {"start": v(157.3, 0) * mm, "end": v(170, 0) * mm});
            skLineSegment(sketch, "E113", {"start": v(170, 0) * mm, "end": v(170, 21.59) * mm});
            skSolve(sketch);
        }
        {
            var Q0;
            Q0=qSketchRegion(id+"F19",true);
            extrude(context, id + "F20", {"entities" : qUnion([Q0]), "operationType" : NewBodyOperationType.ADD, "endBound" : BoundingType.SYMMETRIC, "depth" : 1.9 * mm, "offsetDistance" : 25.4 * mm});
        }
        {
            var Q0;
            Q0=qCreatedBy(makeId("Top.planeOp"),FACE);
            var sketch = newSketch(context, id + "F21", { "sketchPlane" : qUnion([Q0])});
            skCircle(sketch, "E114.0", {"center": v(0, 0) * mm, "radius": 3.18 * mm});
            skCircle(sketch, "E114.1", {"center": v(157.48, -22.86) * mm, "radius": 3.18 * mm});
            skCircle(sketch, "E114.2", {"center": v(157.48, -154.94) * mm, "radius": 3.18 * mm});
            skCircle(sketch, "E114.3", {"center": v(0, -154.94) * mm, "radius": 3.18 * mm});
            skCircle(sketch, "E115", {"center": v(0, 0) * mm, "radius": 1.27 * mm});
            skCircle(sketch, "E116", {"center": v(157.48, -22.86) * mm, "radius": 1.27 * mm});
            skCircle(sketch, "E117", {"center": v(157.48, -154.94) * mm, "radius": 1.27 * mm});
            skCircle(sketch, "E118", {"center": v(0, -154.94) * mm, "radius": 1.27 * mm});
            skLineSegment(sketch, "E119", {"start": v(160.39, -153.67) * mm, "end": v(170, -153.67) * mm});
            skLineSegment(sketch, "E120.0", {"start": v(170, -21.59) * mm, "end": v(170, -24.13) * mm});
            skLineSegment(sketch, "E120.1", {"start": v(-1.27, -166.2) * mm, "end": v(1.27, -166.2) * mm});
            skLineSegment(sketch, "E120.2", {"start": v(-1.27, 16.51) * mm, "end": v(1.27, 16.51) * mm});
            skLineSegment(sketch, "E120.3", {"start": v(-12.7, 1.27) * mm, "end": v(-12.7, -1.27) * mm});
            skLineSegment(sketch, "E121", {"start": v(156.21, -157.85) * mm, "end": v(156.21, -166.2) * mm});
            skLineSegment(sketch, "E122", {"start": v(158.75, -157.85) * mm, "end": v(158.75, -166.2) * mm});
            skPoint(sketch, "E123.orphan", {"position": v(157.48, -153.67) * mm});
            skLineSegment(sketch, "E124.trimOffspring", {"start": v(160.39, -156.2) * mm, "end": v(170, -156.2) * mm});
            skPoint(sketch, "E125.start.orphan", {"position": v(157.48, -156.2) * mm});
            skPoint(sketch, "E126.orphan", {"position": v(158.75, -154.94) * mm});
            skPoint(sketch, "E127.orphan", {"position": v(156.21, -154.94) * mm});
            skLineSegment(sketch, "E128", {"start": v(-2.9, -153.67) * mm, "end": v(-12.7, -153.67) * mm});
            skLineSegment(sketch, "E129", {"start": v(1.27, -157.85) * mm, "end": v(1.27, -166.2) * mm});
            skPoint(sketch, "E130.orphan", {"position": v(0, -153.67) * mm});
            skLineSegment(sketch, "E131.trimOffspring", {"start": v(-2.9, -156.2) * mm, "end": v(-12.7, -156.2) * mm});
            skLineSegment(sketch, "E132.trimOffspring", {"start": v(-1.27, -157.85) * mm, "end": v(-1.27, -166.2) * mm});
            skPoint(sketch, "E133.start.orphan", {"position": v(0, -156.2) * mm});
            skPoint(sketch, "E134.start.orphan", {"position": v(-1.27, -154.94) * mm});
            skPoint(sketch, "E135.orphan", {"position": v(1.27, -154.94) * mm});
            skLineSegment(sketch, "E136", {"start": v(1.27, 2.9) * mm, "end": v(1.27, 16.51) * mm});
            skLineSegment(sketch, "E137", {"start": v(-1.27, 2.9) * mm, "end": v(-1.27, 16.51) * mm});
            skLineSegment(sketch, "E138", {"start": v(-2.9, -1.27) * mm, "end": v(-12.7, -1.27) * mm});
            skLineSegment(sketch, "E139", {"start": v(-2.9, 1.27) * mm, "end": v(-12.7, 1.27) * mm});
            skPoint(sketch, "E140.orphan", {"position": v(0, 1.27) * mm});
            skPoint(sketch, "E141.orphan", {"position": v(-1.27, 0) * mm});
            skPoint(sketch, "E142.orphan", {"position": v(1.27, 0) * mm});
            skPoint(sketch, "E143.orphan", {"position": v(0, -1.27) * mm});
            skLineSegment(sketch, "E144", {"start": v(160.39, -21.59) * mm, "end": v(170, -21.59) * mm});
            skLineSegment(sketch, "E145", {"start": v(160.39, -24.13) * mm, "end": v(170, -24.13) * mm});
            skPoint(sketch, "E146.orphan", {"position": v(157.48, -21.59) * mm});
            skPoint(sketch, "E147.orphan", {"position": v(157.48, -24.13) * mm});
            skPoint(sketch, "E148.orphan", {"position": v(-12.7, 16.51) * mm});
            skLineSegment(sketch, "E149.trimOffspring", {"start": v(-12.7, -153.67) * mm, "end": v(-12.7, -156.2) * mm});
            skPoint(sketch, "E150.orphan", {"position": v(-12.7, -166.2) * mm});
            skLineSegment(sketch, "E151.trimOffspring", {"start": v(156.21, -166.2) * mm, "end": v(158.75, -166.2) * mm});
            skPoint(sketch, "E152.orphan", {"position": v(170, -166.2) * mm});
            skLineSegment(sketch, "E153.trimOffspring", {"start": v(170, -153.67) * mm, "end": v(170, -156.2) * mm});
            skPoint(sketch, "E154.orphan", {"position": v(170, 16.51) * mm});
            skSolve(sketch);
        }
        {
            var Q0;
            Q0=makeQuery(id+"F21.imprint","IMPRINT",FACE,{"disambiguationData":[TD([[makeQuery(id+"F21.imprint","IMPRINT",EDGE,{"derivedFrom":sQuery(id+"F21.wireOp",EDGE,"E120.2")}),-1.0]])]});
            var Q1;
            Q1=makeQuery(id+"F21.imprint","IMPRINT",FACE,{"disambiguationData":[TD([[makeQuery(id+"F21.imprint","IMPRINT",EDGE,{"derivedFrom":sQuery(id+"F21.wireOp",EDGE,"E120.3")}),1.0]])]});
            var Q2;
            Q2=makeQuery(id+"F21.imprint","IMPRINT",FACE,{"disambiguationData":[TD([[makeQuery(id+"F21.imprint","IMPRINT",EDGE,{"derivedFrom":sQuery(id+"F21.wireOp",EDGE,"E115")}),1.0]])]});
            var Q3;
            Q3=makeQuery(id+"F21.imprint","IMPRINT",FACE,{"disambiguationData":[TD([[makeQuery(id+"F21.imprint","IMPRINT",EDGE,{"derivedFrom":sQuery(id+"F21.wireOp",EDGE,"E116")}),1.0]])]});
            var Q4;
            Q4=makeQuery(id+"F21.imprint","IMPRINT",FACE,{"disambiguationData":[TD([[makeQuery(id+"F21.imprint","IMPRINT",EDGE,{"derivedFrom":sQuery(id+"F21.wireOp",EDGE,"E120.0")}),-1.0]])]});
            var Q5;
            Q5=makeQuery(id+"F21.imprint","IMPRINT",FACE,{"disambiguationData":[TD([[makeQuery(id+"F21.imprint","IMPRINT",EDGE,{"derivedFrom":sQuery(id+"F21.wireOp",EDGE,"E117")}),1.0]])]});
            var Q6;
            {var subQ0=sQuery(id+"F21.wireOp",EDGE,"E119");Q6=makeQuery(id+"F21.imprint","IMPRINT",FACE,{"disambiguationData":[TD([[makeQuery(id+"F21.imprint","IMPRINT",EDGE,{"derivedFrom":subQ0}),-1.0]])]});}
            var Q7;
            {var subQ0=sQuery(id+"F21.wireOp",EDGE,"E121");Q7=makeQuery(id+"F21.imprint","IMPRINT",FACE,{"disambiguationData":[TD([[makeQuery(id+"F21.imprint","IMPRINT",EDGE,{"derivedFrom":subQ0}),1.0]])]});}
            var Q8;
            {var subQ0=sQuery(id+"F21.wireOp",EDGE,"E128");Q8=makeQuery(id+"F21.imprint","IMPRINT",FACE,{"disambiguationData":[TD([[makeQuery(id+"F21.imprint","IMPRINT",EDGE,{"derivedFrom":subQ0}),1.0]])]});}
            var Q9;
            Q9=makeQuery(id+"F21.imprint","IMPRINT",FACE,{"disambiguationData":[TD([[makeQuery(id+"F21.imprint","IMPRINT",EDGE,{"derivedFrom":sQuery(id+"F21.wireOp",EDGE,"E118")}),1.0]])]});
            var Q10;
            Q10=makeQuery(id+"F21.imprint","IMPRINT",FACE,{"disambiguationData":[TD([[makeQuery(id+"F21.imprint","IMPRINT",EDGE,{"derivedFrom":sQuery(id+"F21.wireOp",EDGE,"E120.1")}),1.0]])]});
            extrude(context, id + "F22", {"entities" : qUnion([Q0, Q1, Q2, Q3, Q4, Q5, Q6, Q7, Q8, Q9, Q10]), "operationType" : NewBodyOperationType.ADD, "depth" : 12.7 * mm, "offsetDistance" : 25.4 * mm});
        }
        {
            var Q0;
            Q0=makeQuery(id+"F21.imprint","IMPRINT",FACE,{"disambiguationData":[TD([[makeQuery(id+"F21.imprint","IMPRINT",EDGE,{"derivedFrom":sQuery(id+"F21.wireOp",EDGE,"E115")}),-1.0]])]});
            var Q1;
            Q1=makeQuery(id+"F21.imprint","IMPRINT",FACE,{"disambiguationData":[TD([[makeQuery(id+"F21.imprint","IMPRINT",EDGE,{"derivedFrom":sQuery(id+"F21.wireOp",EDGE,"E116")}),-1.0]])]});
            var Q2;
            Q2=makeQuery(id+"F21.imprint","IMPRINT",FACE,{"disambiguationData":[TD([[makeQuery(id+"F21.imprint","IMPRINT",EDGE,{"derivedFrom":sQuery(id+"F21.wireOp",EDGE,"E118")}),-1.0]])]});
            var Q3;
            Q3=makeQuery(id+"F21.imprint","IMPRINT",FACE,{"disambiguationData":[TD([[makeQuery(id+"F21.imprint","IMPRINT",EDGE,{"derivedFrom":sQuery(id+"F21.wireOp",EDGE,"E117")}),-1.0]])]});
            extrude(context, id + "F23", {"entities" : qUnion([Q0, Q1, Q2, Q3]), "operationType" : NewBodyOperationType.ADD, "depth" : 25.4 * mm, "offsetDistance" : 25.4 * mm});
        }
        {
            var Q0;
            Q0=qCreatedBy(makeId("Front.planeOp"),FACE);
            var sketch = newSketch(context, id + "F24", { "sketchPlane" : qUnion([Q0])});
            skLineSegment(sketch, "E155.bottom", {"start": v(166.9, 68.25) * mm, "end": v(7.52, 68.25) * mm});
            skLineSegment(sketch, "E155.top", {"start": v(166.9, 23.16) * mm, "end": v(7.52, 23.16) * mm});
            skLineSegment(sketch, "E155.left", {"start": v(166.9, 68.25) * mm, "end": v(166.9, 23.16) * mm});
            skLineSegment(sketch, "E155.right", {"start": v(7.52, 68.25) * mm, "end": v(7.52, 23.16) * mm});
            skLineSegment(sketch, "E156", {"start": v(156.74, 68.25) * mm, "end": v(156.74, 23.16) * mm, "construction": true});
            skLineSegment(sketch, "E157", {"start": v(155.98, 68.25) * mm, "end": v(155.98, 23.16) * mm, "construction": true});
            skLineSegment(sketch, "E158.1.0.0", {"start": v(144.04, 68.25) * mm, "end": v(144.04, 23.16) * mm, "construction": true});
            skLineSegment(sketch, "E158.1.0.1", {"start": v(143.28, 68.25) * mm, "end": v(143.28, 23.16) * mm, "construction": true});
            skLineSegment(sketch, "E158.2.0.0", {"start": v(131.34, 68.25) * mm, "end": v(131.34, 23.16) * mm, "construction": true});
            skLineSegment(sketch, "E158.2.0.1", {"start": v(130.58, 68.25) * mm, "end": v(130.58, 23.16) * mm, "construction": true});
            skLineSegment(sketch, "E158.3.0.0", {"start": v(118.64, 68.25) * mm, "end": v(118.64, 23.16) * mm, "construction": true});
            skLineSegment(sketch, "E158.3.0.1", {"start": v(117.88, 68.25) * mm, "end": v(117.88, 23.16) * mm, "construction": true});
            skLineSegment(sketch, "E158.4.0.0", {"start": v(105.94, 68.25) * mm, "end": v(105.94, 23.16) * mm, "construction": true});
            skLineSegment(sketch, "E158.4.0.1", {"start": v(105.18, 68.25) * mm, "end": v(105.18, 23.16) * mm, "construction": true});
            skLineSegment(sketch, "E158.5.0.0", {"start": v(93.24, 68.25) * mm, "end": v(93.24, 23.16) * mm, "construction": true});
            skLineSegment(sketch, "E158.5.0.1", {"start": v(92.48, 68.25) * mm, "end": v(92.48, 23.16) * mm, "construction": true});
            skLineSegment(sketch, "E158.6.0.0", {"start": v(80.54, 68.25) * mm, "end": v(80.54, 23.16) * mm, "construction": true});
            skLineSegment(sketch, "E158.6.0.1", {"start": v(79.78, 68.25) * mm, "end": v(79.78, 23.16) * mm, "construction": true});
            skLineSegment(sketch, "E158.7.0.0", {"start": v(67.84, 68.25) * mm, "end": v(67.84, 23.16) * mm, "construction": true});
            skLineSegment(sketch, "E158.7.0.1", {"start": v(67.08, 68.25) * mm, "end": v(67.08, 23.16) * mm, "construction": true});
            skLineSegment(sketch, "E158.8.0.0", {"start": v(55.14, 68.25) * mm, "end": v(55.14, 23.16) * mm, "construction": true});
            skLineSegment(sketch, "E158.8.0.1", {"start": v(54.38, 68.25) * mm, "end": v(54.38, 23.16) * mm, "construction": true});
            skLineSegment(sketch, "E158.9.0.0", {"start": v(42.44, 68.25) * mm, "end": v(42.44, 23.16) * mm, "construction": true});
            skLineSegment(sketch, "E158.9.0.1", {"start": v(41.68, 68.25) * mm, "end": v(41.68, 23.16) * mm, "construction": true});
            skLineSegment(sketch, "E158.10.0.0", {"start": v(29.74, 68.25) * mm, "end": v(29.74, 23.16) * mm, "construction": true});
            skLineSegment(sketch, "E158.10.0.1", {"start": v(28.98, 68.25) * mm, "end": v(28.98, 23.16) * mm, "construction": true});
            skLineSegment(sketch, "E158.11.0.0", {"start": v(17.04, 68.25) * mm, "end": v(17.04, 23.16) * mm, "construction": true});
            skLineSegment(sketch, "E158.11.0.1", {"start": v(16.28, 68.25) * mm, "end": v(16.28, 23.16) * mm, "construction": true});
            skLineSegment(sketch, "E158.direction1", {"start": v(156.74, 23.16) * mm, "end": v(144.04, 23.16) * mm, "construction": true});
            skSolve(sketch);
        }
        {
            var Q0;
            {var subQ0=sQuery(id+"F24.wireOp",EDGE,"E155.right");Q0=makeQuery(id+"F24.imprint","IMPRINT",FACE,{"disambiguationData":[TD([[makeQuery(id+"F24.imprint","IMPRINT",EDGE,{"derivedFrom":subQ0}),1.0]])]});}
            var Q1;
            {var subQ0=sQuery(id+"F24.wireOp",EDGE,"E158.10.0.1");Q1=makeQuery(id+"F24.imprint","IMPRINT",FACE,{"disambiguationData":[TD([[makeQuery(id+"F24.imprint","IMPRINT",EDGE,{"derivedFrom":subQ0}),-1.0]])]});}
            var Q2;
            {var subQ0=sQuery(id+"F24.wireOp",EDGE,"E158.9.0.1");Q2=makeQuery(id+"F24.imprint","IMPRINT",FACE,{"disambiguationData":[TD([[makeQuery(id+"F24.imprint","IMPRINT",EDGE,{"derivedFrom":subQ0}),-1.0]])]});}
            var Q3;
            {var subQ0=sQuery(id+"F24.wireOp",EDGE,"E158.8.0.1");Q3=makeQuery(id+"F24.imprint","IMPRINT",FACE,{"disambiguationData":[TD([[makeQuery(id+"F24.imprint","IMPRINT",EDGE,{"derivedFrom":subQ0}),-1.0]])]});}
            var Q4;
            {var subQ0=sQuery(id+"F24.wireOp",EDGE,"E158.7.0.1");Q4=makeQuery(id+"F24.imprint","IMPRINT",FACE,{"disambiguationData":[TD([[makeQuery(id+"F24.imprint","IMPRINT",EDGE,{"derivedFrom":subQ0}),-1.0]])]});}
            var Q5;
            {var subQ0=sQuery(id+"F24.wireOp",EDGE,"E158.6.0.1");Q5=makeQuery(id+"F24.imprint","IMPRINT",FACE,{"disambiguationData":[TD([[makeQuery(id+"F24.imprint","IMPRINT",EDGE,{"derivedFrom":subQ0}),-1.0]])]});}
            var Q6;
            {var subQ0=sQuery(id+"F24.wireOp",EDGE,"E158.5.0.1");Q6=makeQuery(id+"F24.imprint","IMPRINT",FACE,{"disambiguationData":[TD([[makeQuery(id+"F24.imprint","IMPRINT",EDGE,{"derivedFrom":subQ0}),-1.0]])]});}
            var Q7;
            {var subQ0=sQuery(id+"F24.wireOp",EDGE,"E158.4.0.1");Q7=makeQuery(id+"F24.imprint","IMPRINT",FACE,{"disambiguationData":[TD([[makeQuery(id+"F24.imprint","IMPRINT",EDGE,{"derivedFrom":subQ0}),-1.0]])]});}
            var Q8;
            {var subQ0=sQuery(id+"F24.wireOp",EDGE,"E158.3.0.1");Q8=makeQuery(id+"F24.imprint","IMPRINT",FACE,{"disambiguationData":[TD([[makeQuery(id+"F24.imprint","IMPRINT",EDGE,{"derivedFrom":subQ0}),-1.0]])]});}
            var Q9;
            {var subQ0=sQuery(id+"F24.wireOp",EDGE,"E158.2.0.1");Q9=makeQuery(id+"F24.imprint","IMPRINT",FACE,{"disambiguationData":[TD([[makeQuery(id+"F24.imprint","IMPRINT",EDGE,{"derivedFrom":subQ0}),-1.0]])]});}
            var Q10;
            {var subQ0=sQuery(id+"F24.wireOp",EDGE,"E158.1.0.1");Q10=makeQuery(id+"F24.imprint","IMPRINT",FACE,{"disambiguationData":[TD([[makeQuery(id+"F24.imprint","IMPRINT",EDGE,{"derivedFrom":subQ0}),-1.0]])]});}
            var Q11;
            {var subQ0=sQuery(id+"F24.wireOp",EDGE,"E157");Q11=makeQuery(id+"F24.imprint","IMPRINT",FACE,{"disambiguationData":[TD([[makeQuery(id+"F24.imprint","IMPRINT",EDGE,{"derivedFrom":subQ0}),-1.0]])]});}
            var Q12;
            {var subQ0=sQuery(id+"F24.wireOp",EDGE,"E155.left");Q12=makeQuery(id+"F24.imprint","IMPRINT",FACE,{"disambiguationData":[TD([[makeQuery(id+"F24.imprint","IMPRINT",EDGE,{"derivedFrom":subQ0}),-1.0]])]});}
            extrude(context, id + "F25", {"entities" : qUnion([Q0, Q1, Q2, Q3, Q4, Q5, Q6, Q7, Q8, Q9, Q10, Q11, Q12]), "operationType" : NewBodyOperationType.REMOVE, "oppositeDirection" : true, "depth" : 25.4 * mm, "offsetDistance" : 25.4 * mm});
        }
    });
